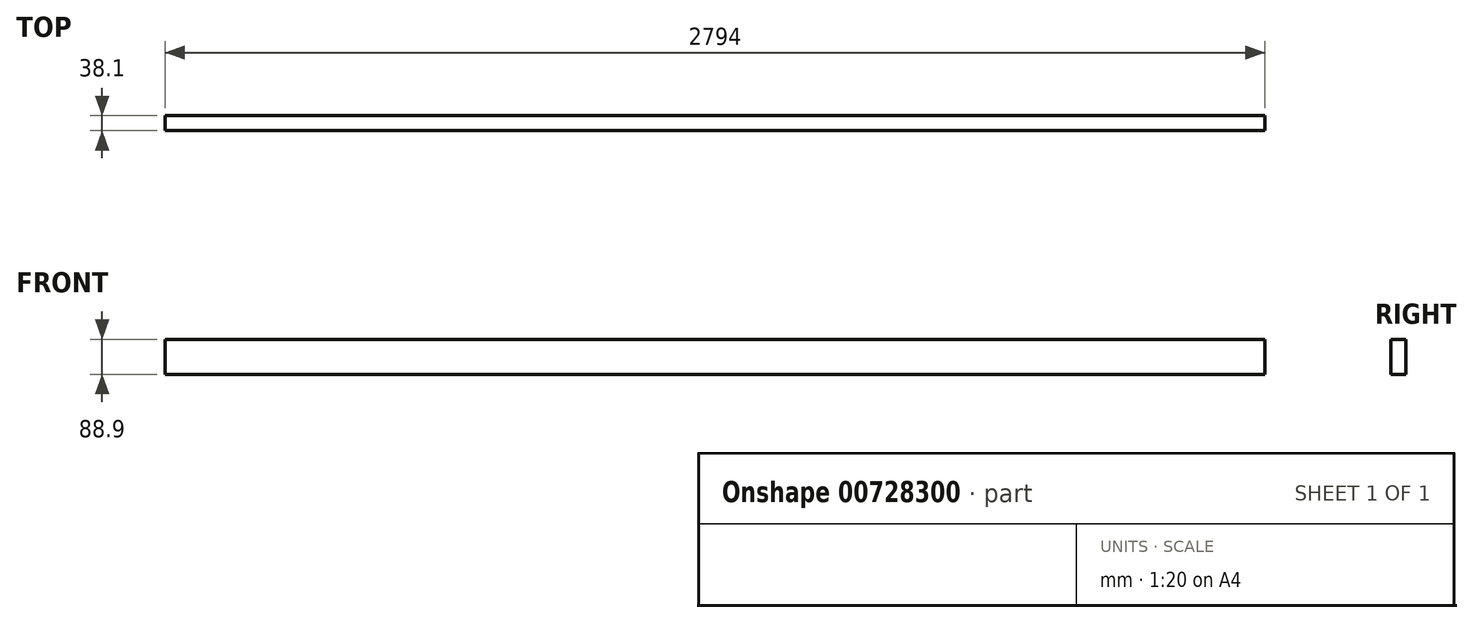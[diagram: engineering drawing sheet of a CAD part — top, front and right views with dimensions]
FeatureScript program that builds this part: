
annotation { "Feature Type Name" : "Feature", "Feature Type Description" : "" }
export const myFeature = defineFeature(function(context is Context, id is Id, definition is map)
    precondition{}
    {
        {
            var Q0;
            Q0=qCreatedBy(makeId("Front.planeOp"),FACE);
            var sketch = newSketch(context, id + "F0", { "sketchPlane" : qUnion([Q0])});
            skLineSegment(sketch, "E0.bottom", {"start": v(-1397, -44.45) * mm, "end": v(1397, -44.45) * mm});
            skLineSegment(sketch, "E0.top", {"start": v(-1397, 44.45) * mm, "end": v(1397, 44.45) * mm});
            skLineSegment(sketch, "E0.left", {"start": v(-1397, -44.45) * mm, "end": v(-1397, 44.45) * mm});
            skLineSegment(sketch, "E0.right", {"start": v(1397, -44.45) * mm, "end": v(1397, 44.45) * mm});
            skPoint(sketch, "E0.middle", {"position": v(0, 0) * mm});
            skSolve(sketch);
        }
        {
            var Q0;
            Q0=qSketchRegion(id+"F0",true);
            extrude(context, id + "F1", {"entities" : qUnion([Q0]), "depth" : 38.1 * mm, "offsetDistance" : 25.4 * mm});
        }
    });
